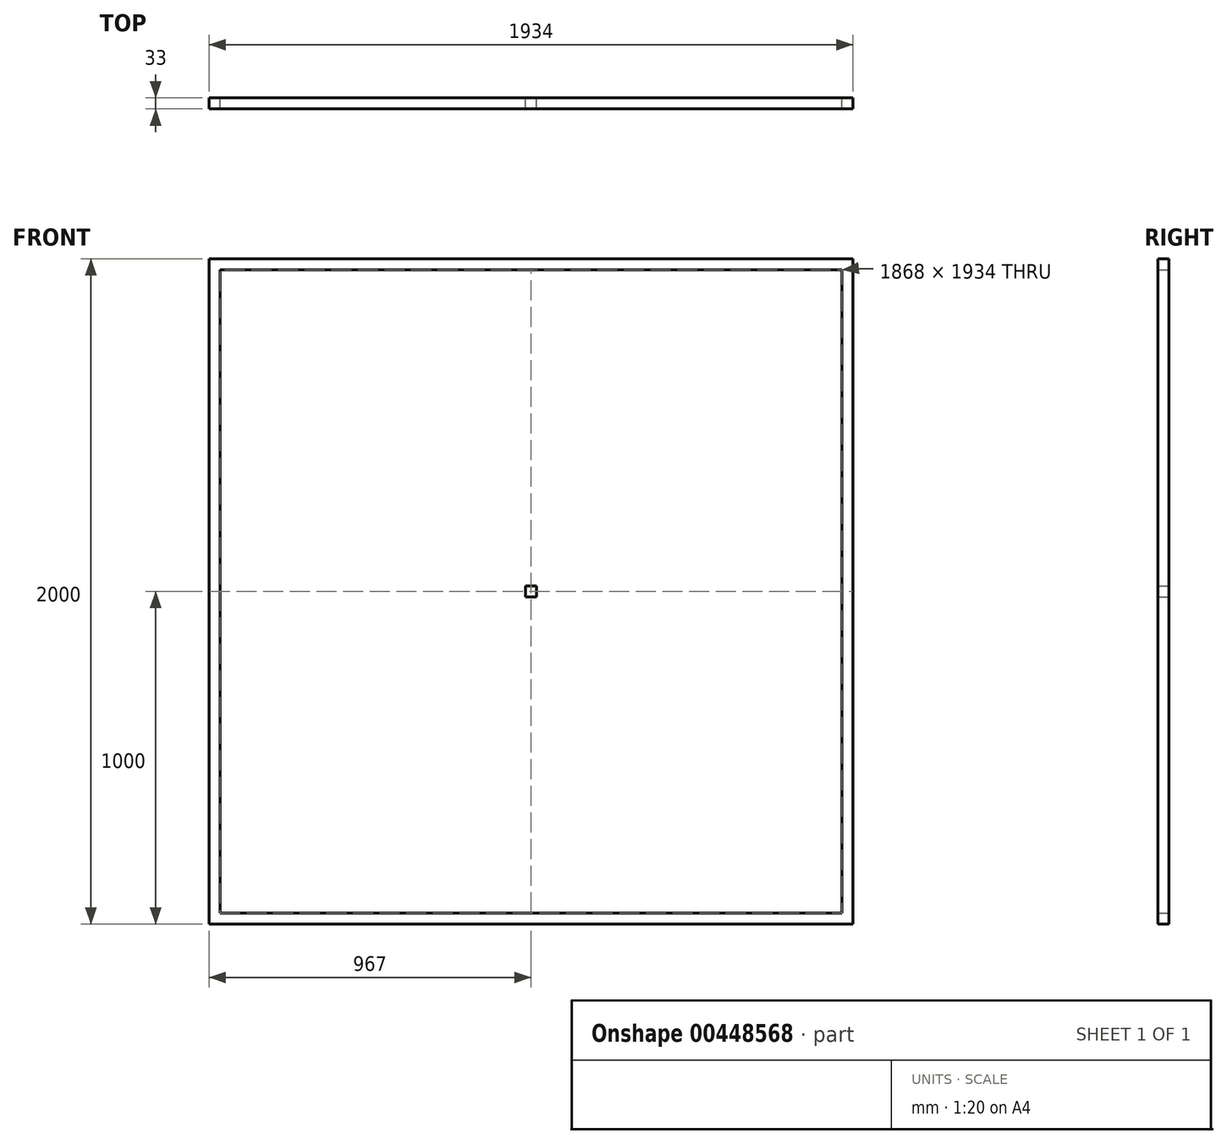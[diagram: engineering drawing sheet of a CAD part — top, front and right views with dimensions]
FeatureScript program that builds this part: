
annotation { "Feature Type Name" : "Feature", "Feature Type Description" : "" }
export const myFeature = defineFeature(function(context is Context, id is Id, definition is map)
    precondition{}
    {
        {
            var Q0;
            Q0=qCreatedBy(makeId("Front.planeOp"),FACE);
            var sketch = newSketch(context, id + "F0", { "sketchPlane" : qUnion([Q0])});
            skLineSegment(sketch, "E0.bottom", {"start": v(0, 0) * mm, "end": v(1934, 0) * mm});
            skLineSegment(sketch, "E0.top", {"start": v(0, 2000) * mm, "end": v(1934, 2000) * mm});
            skLineSegment(sketch, "E0.left", {"start": v(0, 0) * mm, "end": v(0, 2000) * mm});
            skLineSegment(sketch, "E0.right", {"start": v(1934, 0) * mm, "end": v(1934, 2000) * mm});
            skLineSegment(sketch, "E1.0", {"start": v(33, 33) * mm, "end": v(33, 1967) * mm});
            skLineSegment(sketch, "E1.1", {"start": v(33, 33) * mm, "end": v(1901, 33) * mm});
            skLineSegment(sketch, "E1.2", {"start": v(1901, 33) * mm, "end": v(1901, 1967) * mm});
            skLineSegment(sketch, "E1.3", {"start": v(33, 1967) * mm, "end": v(1901, 1967) * mm});
            skLineSegment(sketch, "E2.bottom", {"start": v(950.5, 1967) * mm, "end": v(983.5, 1967) * mm});
            skLineSegment(sketch, "E2.top", {"start": v(950.5, 33) * mm, "end": v(983.5, 33) * mm});
            skLineSegment(sketch, "E2.left", {"start": v(950.5, 1967) * mm, "end": v(950.5, 33) * mm});
            skLineSegment(sketch, "E2.right", {"start": v(983.5, 1967) * mm, "end": v(983.5, 33) * mm});
            skLineSegment(sketch, "E3.bottom", {"start": v(33, 1016.5) * mm, "end": v(1901, 1016.5) * mm});
            skLineSegment(sketch, "E3.top", {"start": v(33, 983.5) * mm, "end": v(1901, 983.5) * mm});
            skLineSegment(sketch, "E3.left", {"start": v(33, 1016.5) * mm, "end": v(33, 983.5) * mm});
            skLineSegment(sketch, "E3.right", {"start": v(1901, 1016.5) * mm, "end": v(1901, 983.5) * mm});
            skSolve(sketch);
        }
        {
            var Q0;
            Q0 = qSketchRegion(id + "F0", true);
            var Q1;
            {var subQ5=sQuery(id+"F0.wireOp",EDGE,"E3.left");Q1=makeQuery(id+"F0.imprint","IMPRINT",FACE,{"disambiguationData":[TD([[makeQuery(id+"F0.imprint","IMPRINT",EDGE,{"derivedFrom":subQ5}),1.0]])]});}
            var Q2;
            {var subQ5=sQuery(id+"F0.wireOp",EDGE,"E3.right");Q2=makeQuery(id+"F0.imprint","IMPRINT",FACE,{"disambiguationData":[TD([[makeQuery(id+"F0.imprint","IMPRINT",EDGE,{"derivedFrom":subQ5}),-1.0]])]});}
            var Q3;
            {var subQ0=sQuery(id+"F0.wireOp",EDGE,"E2.top");Q3=makeQuery(id+"F0.imprint","IMPRINT",FACE,{"disambiguationData":[TD([[makeQuery(id+"F0.imprint","IMPRINT",EDGE,{"derivedFrom":subQ0}),1.0]])]});}
            var Q4;
            {var subQ0=sQuery(id+"F0.wireOp",EDGE,"E3.bottom");var subQ1=sQuery(id+"F0.wireOp",EDGE,"E2.left");var subQ2=makeQuery(id+"F0.imprint","INTERSECT",VERTEX,{"derivedFrom":[subQ1,subQ0]});Q4=makeQuery(id+"F0.imprint","IMPRINT",FACE,{"disambiguationData":[TD([[makeQuery(id+"F0.imprint","IMPRINT",EDGE,{"disambiguationData":[TD([[subQ2,-1.0]])],"derivedFrom":subQ1}),1.0]])]});}
            var Q5;
            {var subQ0=sQuery(id+"F0.wireOp",EDGE,"E2.bottom");Q5=makeQuery(id+"F0.imprint","IMPRINT",FACE,{"disambiguationData":[TD([[makeQuery(id+"F0.imprint","IMPRINT",EDGE,{"derivedFrom":subQ0}),-1.0]])]});}
            extrude(context, id + "F1", {"entities" : qUnion([Q0, Q1, Q2, Q3, Q4, Q5]), "depth" : 33 * mm});
        }
    });
